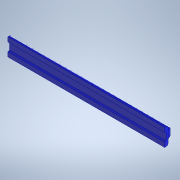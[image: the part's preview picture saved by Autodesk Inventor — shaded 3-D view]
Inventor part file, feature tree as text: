
AUTODESK INVENTOR PART (.ipt)
format: ipt  version: 2020.3 (Build 243373000, 373)  size: 201,216 bytes
history: native  units: mm (DEFAULTED — no unit token found)
features: extrude x2, sketch x2, pattern_linear x1
ambient origin geometry x8: Origin, YZ Plane, XZ Plane, XY Plane, X Axis, Y Axis, Z Axis, Center Point
bodies: Solid1 (feature_tree)
feature tree (5):
  extrude  "Extrusion1"  Depth=5.0mm TaperAngle=0.0deg
  extrude  "Extrusion2"  [1 undecoded]
  pattern_linear  "Rectangular Pattern1"  [2 undecoded]
  sketch  "Sketch_1"  dims[d0=90.0mm d1=0.0mm d2=5.0mm d3=0.0mm]
  sketch  "Sketch_5"  dims[d4=6410.0mm d6=3.14159mm d7=10.0mm d9=0.0mm]
note: 3 required parameter values undecoded (feature->parameter linkage not recoverable at this tier; creation-order binding heuristic only, values carry confidence <= 0.55)
